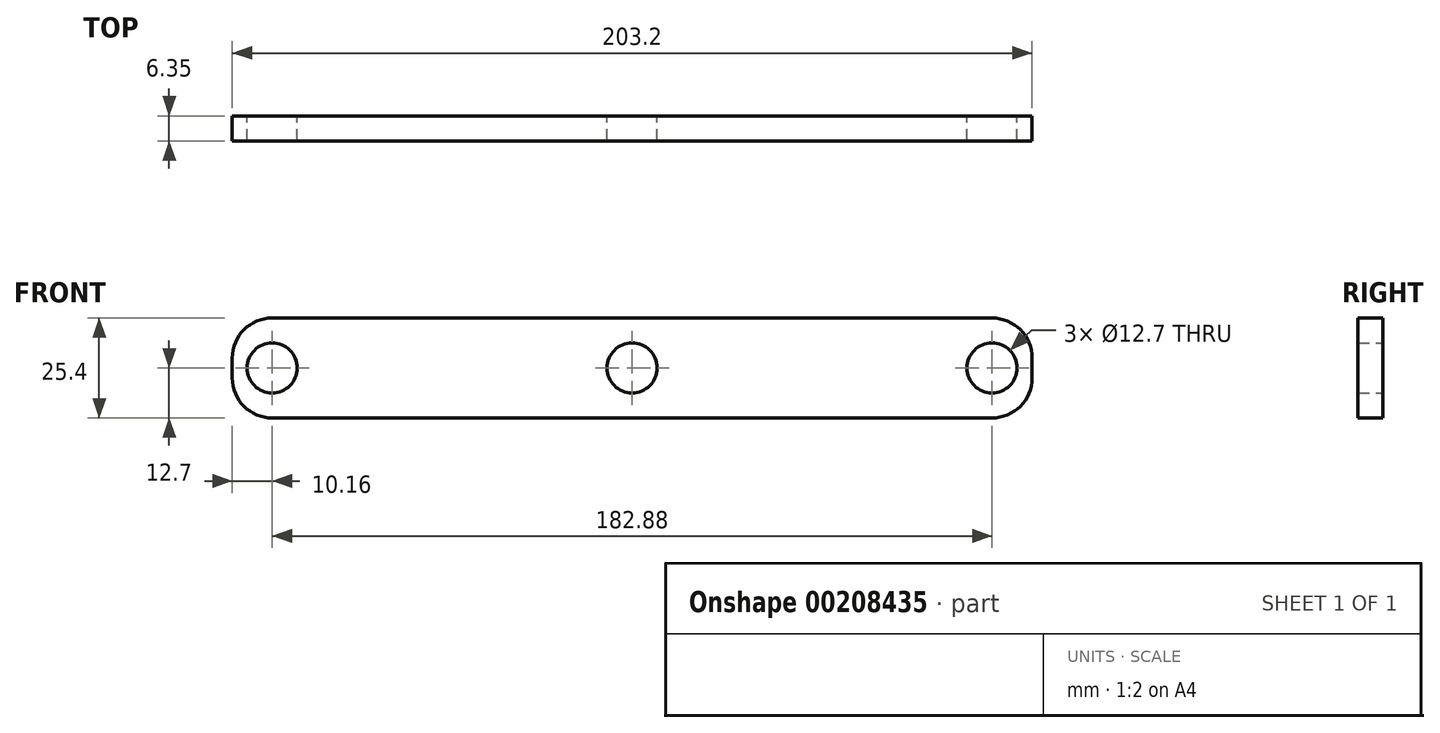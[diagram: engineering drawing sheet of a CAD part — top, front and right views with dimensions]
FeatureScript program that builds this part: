
annotation { "Feature Type Name" : "Feature", "Feature Type Description" : "" }
export const myFeature = defineFeature(function(context is Context, id is Id, definition is map)
    precondition{}
    {
        {
            var Q0;
            Q0=qCreatedBy(makeId("Front.planeOp"),FACE);
            var sketch = newSketch(context, id + "F0", { "sketchPlane" : qUnion([Q0])});
            skLineSegment(sketch, "E0.bottom", {"start": v(91.44, 12.7) * mm, "end": v(-91.44, 12.7) * mm});
            skLineSegment(sketch, "E0.top", {"start": v(91.44, -12.7) * mm, "end": v(-91.44, -12.7) * mm});
            skLineSegment(sketch, "E0.left", {"start": v(101.6, 2.54) * mm, "end": v(101.6, -2.54) * mm});
            skLineSegment(sketch, "E0.right", {"start": v(-101.6, 2.54) * mm, "end": v(-101.6, -2.54) * mm});
            skPoint(sketch, "E0.middle", {"position": v(0, 0) * mm});
            skPoint(sketch, "E1.visualSharp", {"position": v(-101.6, 12.7) * mm});
            skArc(sketch, "E1.filletArc", {"start": v(-91.44, 12.7) * mm, "mid": v(-98.62, 9.72) * mm, "end": v(-101.6, 2.54) * mm});
            skPoint(sketch, "E2.visualSharp", {"position": v(-101.6, -12.7) * mm});
            skArc(sketch, "E2.filletArc", {"start": v(-101.6, -2.54) * mm, "mid": v(-98.62, -9.72) * mm, "end": v(-91.44, -12.7) * mm});
            skPoint(sketch, "E3.visualSharp", {"position": v(101.6, 12.7) * mm});
            skArc(sketch, "E3.filletArc", {"start": v(101.6, 2.54) * mm, "mid": v(98.62, 9.72) * mm, "end": v(91.44, 12.7) * mm});
            skPoint(sketch, "E4.visualSharp", {"position": v(101.6, -12.7) * mm});
            skArc(sketch, "E4.filletArc", {"start": v(91.44, -12.7) * mm, "mid": v(98.62, -9.72) * mm, "end": v(101.6, -2.54) * mm});
            skCircle(sketch, "E5", {"center": v(-91.44, 0) * mm, "radius": 6.35 * mm});
            skCircle(sketch, "E6", {"center": v(91.44, 0) * mm, "radius": 6.35 * mm});
            skCircle(sketch, "E7", {"center": v(0, 0) * mm, "radius": 6.35 * mm});
            skSolve(sketch);
        }
        {
            var Q0;
            Q0=qSketchRegion(id+"F0",true);
            extrude(context, id + "F1", {"entities" : qUnion([Q0]), "depth" : 6.35 * mm});
        }
    });
